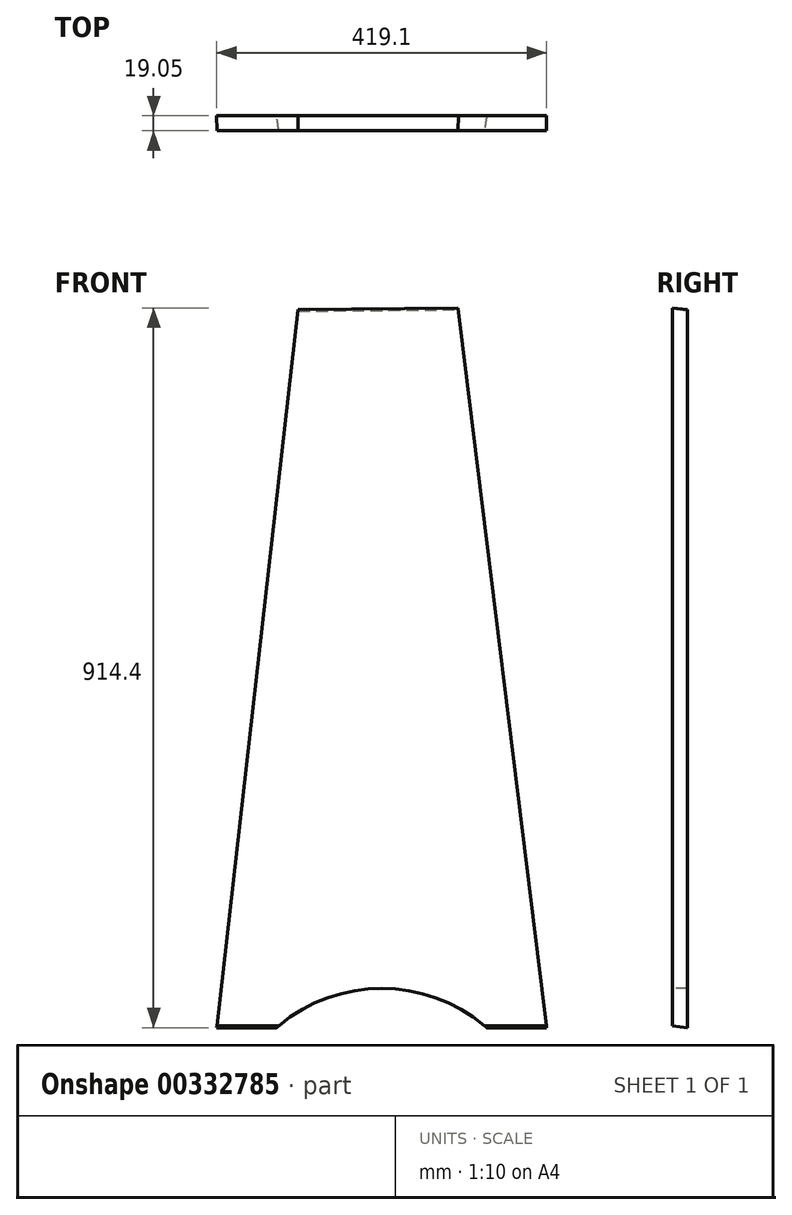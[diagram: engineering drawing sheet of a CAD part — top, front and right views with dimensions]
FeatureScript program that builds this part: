
annotation { "Feature Type Name" : "Feature", "Feature Type Description" : "" }
export const myFeature = defineFeature(function(context is Context, id is Id, definition is map)
    precondition{}
    {
        {
            var Q0;
            Q0=qCreatedBy(makeId("Front.planeOp"),FACE);
            var sketch = newSketch(context, id + "F0", { "sketchPlane" : qUnion([Q0])});
            skLineSegment(sketch, "E0", {"start": v(103.63, 912.55) * mm, "end": v(0, 0) * mm});
            skLineSegment(sketch, "E1", {"start": v(0, 0) * mm, "end": v(419.1, 0) * mm});
            skLineSegment(sketch, "E2", {"start": v(419.1, 0) * mm, "end": v(306.83, 914.4) * mm});
            skLineSegment(sketch, "E3", {"start": v(306.83, 914.4) * mm, "end": v(103.63, 912.55) * mm});
            skSolve(sketch);
        }
        {
            var Q0;
            Q0=makeQuery(id+"F0.imprint","IMPRINT",FACE,{"disambiguationData":[TD([[makeQuery(id+"F0.imprint","IMPRINT",EDGE,{"derivedFrom":sQuery(id+"F0.wireOp",EDGE,"E0")}),1.0]])]});
            extrude(context, id + "F1", {"entities" : qUnion([Q0]), "depth" : 19.05 * mm});
        }
        {
            var Q0;
            Q0=makeQuery(id+"F1.opExtrude","CAP_FACE",FACE,{"disambiguationData":[OSD([sQuery(id+"F0.wireOp",EDGE,"E0"),sQuery(id+"F0.wireOp",EDGE,"E1"),sQuery(id+"F0.wireOp",EDGE,"E2"),sQuery(id+"F0.wireOp",EDGE,"E3")])],"isStart":false});
            var sketch = newSketch(context, id + "F2", { "sketchPlane" : qUnion([Q0])});
            skArc(sketch, "E4", {"start": v(342.9, 0) * mm, "mid": v(209.55, 49.88) * mm, "end": v(76.2, 0) * mm});
            skSolve(sketch);
        }
        {
            var Q0;
            {var subQ0=sQuery(id+"F2.wireOp",EDGE,"E4");Q0=makeQuery(id+"F2.imprint","IMPRINT",FACE,{"disambiguationData":[TD([[makeQuery(id+"F2.imprint","IMPRINT",EDGE,{"derivedFrom":subQ0}),1.0]])]});}
            extrude(context, id + "F3", {"entities" : qUnion([Q0]), "operationType" : NewBodyOperationType.REMOVE, "oppositeDirection" : true, "depth" : 19.05 * mm});
        }
        {
            var Q0;
            Q0=qCreatedBy(makeId("Right.planeOp"),FACE);
            var sketch = newSketch(context, id + "F4", { "sketchPlane" : qUnion([Q0])});
            skLineSegment(sketch, "E5", {"start": v(-19.05, 0) * mm, "end": v(0, 0) * mm});
            skLineSegment(sketch, "E6", {"start": v(0, 0) * mm, "end": v(-19.05, 2.34) * mm});
            skLineSegment(sketch, "E7", {"start": v(-19.05, 2.34) * mm, "end": v(-19.05, 0) * mm});
            skSolve(sketch);
        }
        {
            var Q0;
            Q0 = qSketchRegion(id + "F4", true);
            extrude(context, id + "F5", {"entities" : qUnion([Q0]), "operationType" : NewBodyOperationType.REMOVE, "depth" : 419.1 * mm});
        }
        {
            var Q0;
            Q0=makeQuery(id+"F1.opExtrude","CAP_EDGE",EDGE,{"disambiguationData":[OSD([sQuery(id+"F0.wireOp",EDGE,"E3")])],"isStart":true});
            chamfer(context, id + "F6", {"entities" : qUnion([Q0]), "chamferType" : ChamferType.OFFSET_ANGLE, "width" : 19.05 * mm, "oppositeDirection" : false, "angle" : 7 * degree, "tangentPropagation" : true});
        }
    });
